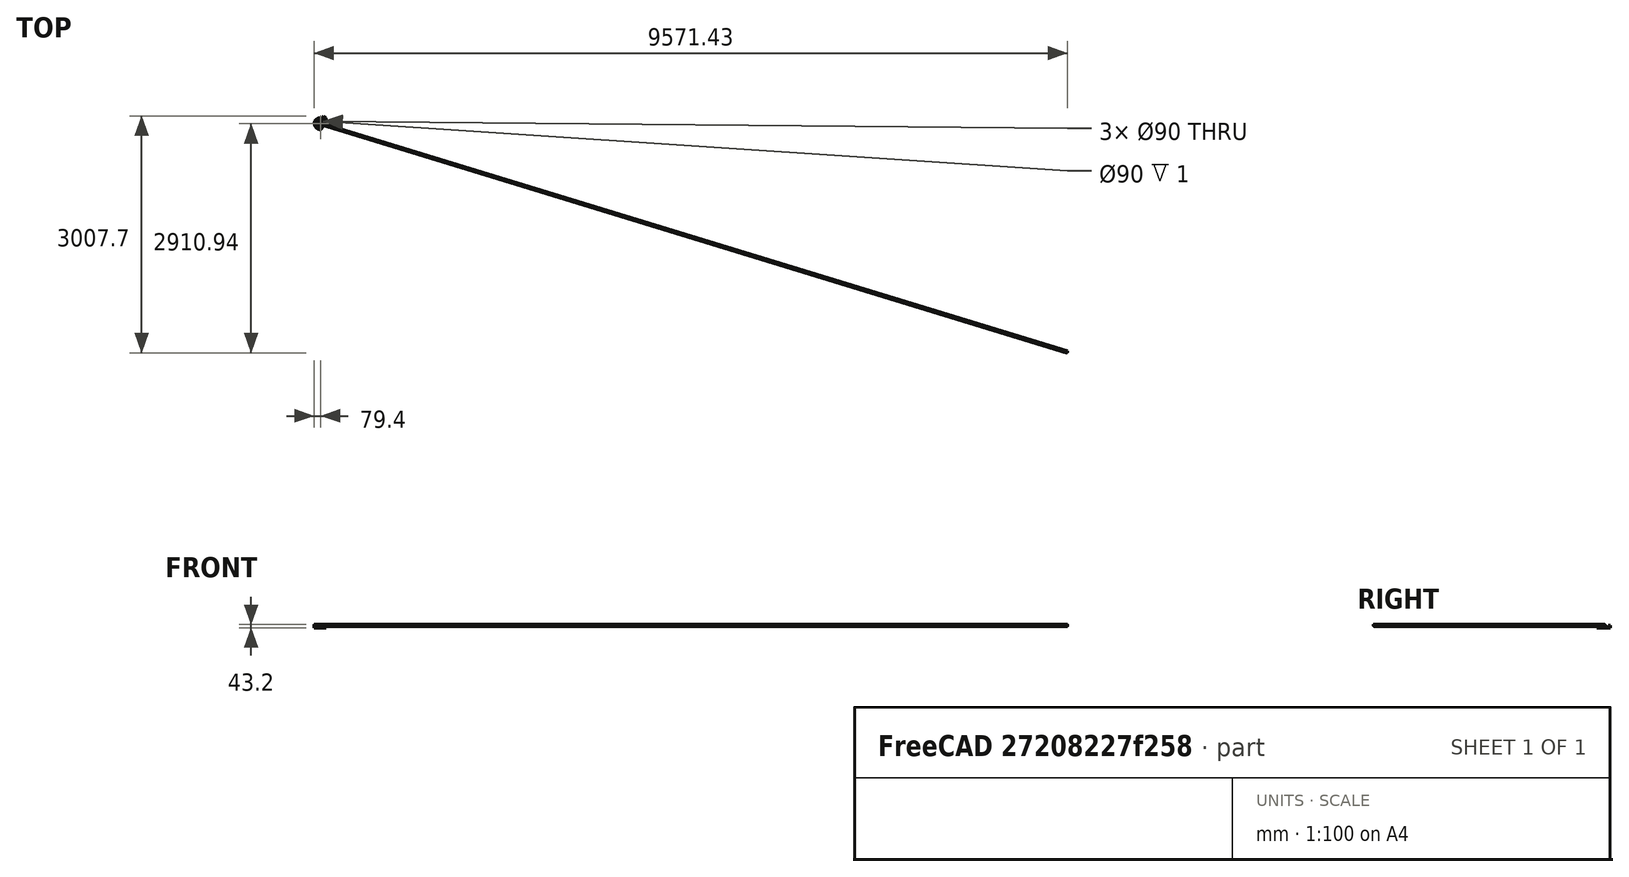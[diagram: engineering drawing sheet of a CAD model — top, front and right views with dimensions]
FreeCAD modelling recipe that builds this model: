
FCSTD DOCUMENT  (FreeCAD 0.16R)
Label: chainguard30tV2
License: All rights reserved
LicenseURL: http://en.wikipedia.org/wiki/All_rights_reserved
objects: Sketcher::SketchObject×7, PartDesign::Pad×5, PartDesign::Pocket×2, Part::FeaturePython×2, Mesh::Feature×2
note: 23 computed .brp shape members not serialized (recipe doc carries the construction recipe); baked Part::Feature solids carry a one-line shape summary decoded from their .brp

FEATURE [Sketcher::SketchObject] Sketch001
  sketch-geometry (6):
    g0: LineSegment StartX=50 StartY=74 StartZ=0 EndX=0 EndY=74 EndZ=0
    g1: LineSegment StartX=73 StartY=0 StartZ=0 EndX=0 EndY=-74 EndZ=0
    g2: ArcOfCircle CenterX=-1.20229e-07 CenterY=0 CenterZ=0 NormalX=0 NormalY=0 NormalZ=1 Radius=74 StartAngle=1.5708 EndAngle=4.71239
    g3: Circle CenterX=0 CenterY=0 CenterZ=0 NormalX=0 NormalY=0 NormalZ=1 Radius=45
    g4: LineSegment StartX=73 StartY=51 StartZ=0 EndX=73 EndY=0 EndZ=0
    g5: ArcOfCircle CenterX=50 CenterY=51 CenterZ=0 NormalX=0 NormalY=0 NormalZ=1 Radius=23 StartAngle=0 EndAngle=1.5708
  constraints (18):
    c: Horizontal(g0)
    c: Coincident(g2,g1)
    c: Coincident(g0,g2)
    c: DistanceX(g1,g0) = 0
    c: DistanceY(g1,g0) = 148
    c: Symmetric(g1,g0,g-1)
    c: Radius(g3) = 45
    c: Coincident(g3,g-1)
    c: DistanceX(g0,g0) = 50
    c: Vertical(g4)
    c: DistanceX(g-1,g4) = 73
    c: Coincident(g5,g4)
    c: Coincident(g5,g0)
    c: Radius(g5) = 23
    c: Radius(g2) = 74
    c: DistanceY(g4,g0) = 23
    c: Coincident(g1,g4)
    c: PointOnObject(g1,g-1)
FEATURE [PartDesign::Pad] Pad  label="Faceplate"
  Length = 1
  Length2 = 100
  Reversed = true
  Sketch = -> Sketch001
  Type = 0
FEATURE [Sketcher::SketchObject] Sketch002
  sketch-geometry (6):
    g0: LineSegment StartX=50 StartY=74 StartZ=0 EndX=0 EndY=74 EndZ=0
    g1: ArcOfCircle CenterX=-9.32425e-05 CenterY=0 CenterZ=0 NormalX=0 NormalY=0 NormalZ=1 Radius=74 StartAngle=1.5708 EndAngle=4.71239
    g2: LineSegment StartX=0 StartY=72 StartZ=0 EndX=50 EndY=72 EndZ=0
    g3: LineSegment StartX=50 StartY=74 StartZ=0 EndX=50 EndY=72 EndZ=0
    g4: ArcOfCircle CenterX=8.69593e-07 CenterY=0 CenterZ=0 NormalX=0 NormalY=0 NormalZ=1 Radius=72 StartAngle=1.5708 EndAngle=4.71239
    g5: LineSegment StartX=0 StartY=-74 StartZ=0 EndX=0 EndY=-72 EndZ=0
  constraints (18):
    c: Horizontal(g0)
    c: Coincident(g0,g1)
    c: DistanceX(g1,g0) = 0
    c: DistanceY(g1,g0) = 148
    c: Symmetric(g1,g0,g-1)
    c: Parallel(g0,g2)
    c: DistanceY(g2,g0) = 2
    c: DistanceX(g0,g2) = 0
    c: DistanceX(g4) = 0
    c: DistanceX(g0) = 50
    c: Equal(g2,g0)
    c: Coincident(g3,g2)
    c: Coincident(g3,g0)
    c: Coincident(g4,g2)
    c: Radius(g4) = 72
    c: Radius(g1) = 74
    c: Coincident(g5,g4)
    c: Coincident(g5,g1)
FEATURE [PartDesign::Pad] Pad001  label="Connector"
  Length = 6
  Length2 = 100
  Sketch = -> Sketch002
  Type = 0
FEATURE [Sketcher::SketchObject] Sketch024  label="FaceStiffener"
  sketch-geometry (6):
    g0: ArcOfCircle CenterX=0 CenterY=0 CenterZ=0 NormalX=0 NormalY=0 NormalZ=1 Radius=48 StartAngle=1.34179 EndAngle=4.9414
    g1: Circle CenterX=0 CenterY=0 CenterZ=0 NormalX=0 NormalY=0 NormalZ=1 Radius=45
    g2: LineSegment StartX=10.8966 StartY=46.7468 StartZ=0 EndX=70 EndY=36.8563 EndZ=0
    g3: LineSegment StartX=70 StartY=1.4435 StartZ=0 EndX=37.1106 EndY=-33.5618 EndZ=0
    g4: LineSegment StartX=37.1106 StartY=-33.5618 StartZ=0 EndX=10.8966 EndY=-46.7468 EndZ=0
    g5: LineSegment StartX=70 StartY=36.8563 StartZ=0 EndX=70 EndY=1.4435 EndZ=0
  constraints (17):
    c: Coincident(g0,g-1)
    c: Radius(g0) = 48
    c: Coincident(g1,g-1)
    c: Radius(g1) = 45
    c: Coincident(g3,g4)
    c: Coincident(g0,g2)
    c: DistanceX(g-1,g2) = 70
    c: DistanceY(g-1,g0) = 46.7468
    c: DistanceX(g0) = 10.8966
    c: Coincident(g4,g0)
    c: Coincident(g5,g2)
    c: Coincident(g5,g3)
    c: Vertical(g5)
    c: Distance(g4) = 29.3431
    c: Distance(g3) = 48.0321
    c: Distance(g5) = 35.4128
    c: Distance(g2) = 59.9252
FEATURE [PartDesign::Pad] Pad002  label="FaceStiffener001"
  Length = 1
  Length2 = 100
  Sketch = -> Sketch024
  Type = 0
FEATURE [Sketcher::SketchObject] Sketch
  Support = -> Pad [Face7]
  sketch-geometry (5):
    g0: LineSegment [constr] StartX=-4 StartY=2 StartZ=0 EndX=53.3173 EndY=86.9764 EndZ=0
    g1: LineSegment StartX=22.2526 StartY=72.2162 StartZ=0 EndX=64.4703 EndY=72.2162 EndZ=0
    g2: LineSegment StartX=64.4703 StartY=72.2162 StartZ=0 EndX=67.8254 EndY=77.1905 EndZ=0
    g3: LineSegment StartX=67.8254 StartY=77.1905 StartZ=0 EndX=38.8091 EndY=96.7622 EndZ=0
    g4: LineSegment StartX=38.8091 StartY=96.7622 StartZ=0 EndX=22.2526 EndY=72.2162 EndZ=0
  constraints (15):
    c: DistanceY(g-1,g0) = 2
    c: DistanceX(g0,g-1) = 4
    c: Angle(g0) = 0.977384
    c: Distance(g0) = 102.5
    c: Horizontal(g1)
    c: Coincident(g1,g2)
    c: Coincident(g2,g3)
    c: Coincident(g3,g4)
    c: Coincident(g1,g4)
    c: Parallel(g2,g0)
    c: Parallel(g0,g4)
    c: Distance(g2) = 6
    c: Symmetric(g3,g2,g0)
    c: Distance(g3) = 35
    c: PointOnObject(g0,g3)
FEATURE [PartDesign::Pad] Pad003  label="STBoss"
  Length = 31
  Length2 = 1
  Sketch = -> Sketch
  Type = 4
FEATURE [Sketcher::SketchObject] Sketch025
  Support = -> Pad003 [Face4]
  sketch-geometry (5):
    g0: LineSegment [constr] StartX=-4 StartY=2 StartZ=0 EndX=-74.2884 EndY=23.4893 EndZ=0
    g1: LineSegment StartX=-69.1719 StartY=40.2247 StartZ=0 EndX=-79.4049 EndY=6.75399 EndZ=0
    g2: LineSegment StartX=-79.4049 StartY=6.75399 StartZ=0 EndX=-73.6671 EndY=4.99976 EndZ=0
    g3: LineSegment StartX=-73.6671 StartY=4.99976 StartZ=0 EndX=-63.4341 EndY=38.4704 EndZ=0
    g4: LineSegment StartX=-63.4341 StartY=38.4704 StartZ=0 EndX=-69.1719 EndY=40.2247 EndZ=0
  constraints (16):
    c: DistanceY(g-1,g0) = 2
    c: DistanceX(g0,g-1) = 4
    c: Angle(g0) = 2.84489
    c: Coincident(g1,g2)
    c: Coincident(g2,g3)
    c: Coincident(g3,g4)
    c: Coincident(g4,g1)
    c: Distance(g4) = 6
    c: Parallel(g2,g0)
    c: Parallel(g0,g4)
    c: Equal(g4,g2)
    c: Perpendicular(g0,g1)
    c: PointOnObject(g0,g1)
    c: Symmetric(g1,g1,g0)
    c: Distance(g0) = 73.5
    c: Distance(g1) = 35
FEATURE [PartDesign::Pad] Pad004
  Length = 31
  Length2 = 1
  Sketch = -> Sketch025
  Type = 4
FEATURE [Sketcher::SketchObject] Sketch026
  ExternalGeometry = -> [Pad004]
  Placement = pos=(-74.5057,22.7787,0) rot=(-0.463605,0.626526,0.626526;4.00981rad)
  Support = -> Pad004 [Face21]
  sketch-geometry (1):
    g0: Circle CenterX=-0.743123 CenterY=31 CenterZ=0 NormalX=0 NormalY=0 NormalZ=1 Radius=11.2
  constraints (2):
    c: Symmetric(g-3,g-4,g0)
    c: Radius(g0) = 11.2
FEATURE [PartDesign::Pocket] Pocket
  Length = 5
  Sketch = -> Sketch026
  Type = 1
FEATURE [Sketcher::SketchObject] Sketch027
  ExternalGeometry = -> [Pocket]
  Placement = pos=(56.9937,84.4966,0) rot=(0.211303,0.691141,0.691141;2.72511rad)
  Support = -> Pocket [Face25]
  sketch-geometry (1):
    g0: Circle CenterX=4.43454 CenterY=31 CenterZ=0 NormalX=0 NormalY=0 NormalZ=1 Radius=11.2
  constraints (2):
    c: Symmetric(g-3,g-4,g0)
    c: Radius(g0) = 11.2
FEATURE [PartDesign::Pocket] Pocket001
  Length = 5
  Sketch = -> Sketch027
  Type = 1
FEATURE [Part::FeaturePython] refine  label="refine_Connector"  # WARN: FeaturePython — macro-defined, semantics opaque (R4)
  Base = -> Pad001
FEATURE [Part::FeaturePython] refine001  label="refine_Pocket001"  # WARN: FeaturePython — macro-defined, semantics opaque (R4)
  Base = -> Pocket001
FEATURE [Mesh::Feature] Mesh  label="refine_Connector (Meshed)"
FEATURE [Mesh::Feature] Mesh001  label="refine_Pocket001 (Meshed)"
